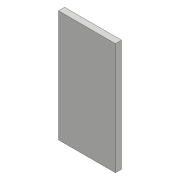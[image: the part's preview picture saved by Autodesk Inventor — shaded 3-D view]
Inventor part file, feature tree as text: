
AUTODESK INVENTOR PART (.ipt)
format: ipt  version: 2018 (Build 220112000, 112)  size: 81,408 bytes
history: native  units: mm
features: extrude x2, sketch x2
ambient origin geometry x8: Origin, YZ Plane, XZ Plane, XY Plane, X Axis, Y Axis, Z Axis, Center Point
bodies: Solid1 (feature_tree)
feature tree (4):
  extrude  "Extrusion1"  Depth=28.0mm
  extrude  "Extrusion2"  Depth=43.5mm
  sketch  "Sketch1"  dims[d0=55.0mm d1=28.0mm]
  sketch  "Sketch2"  dims[d2=3.0mm d3=0.0mm d4=43.5mm d5=21.5mm d6=1.6mm d7=0.0mm]
